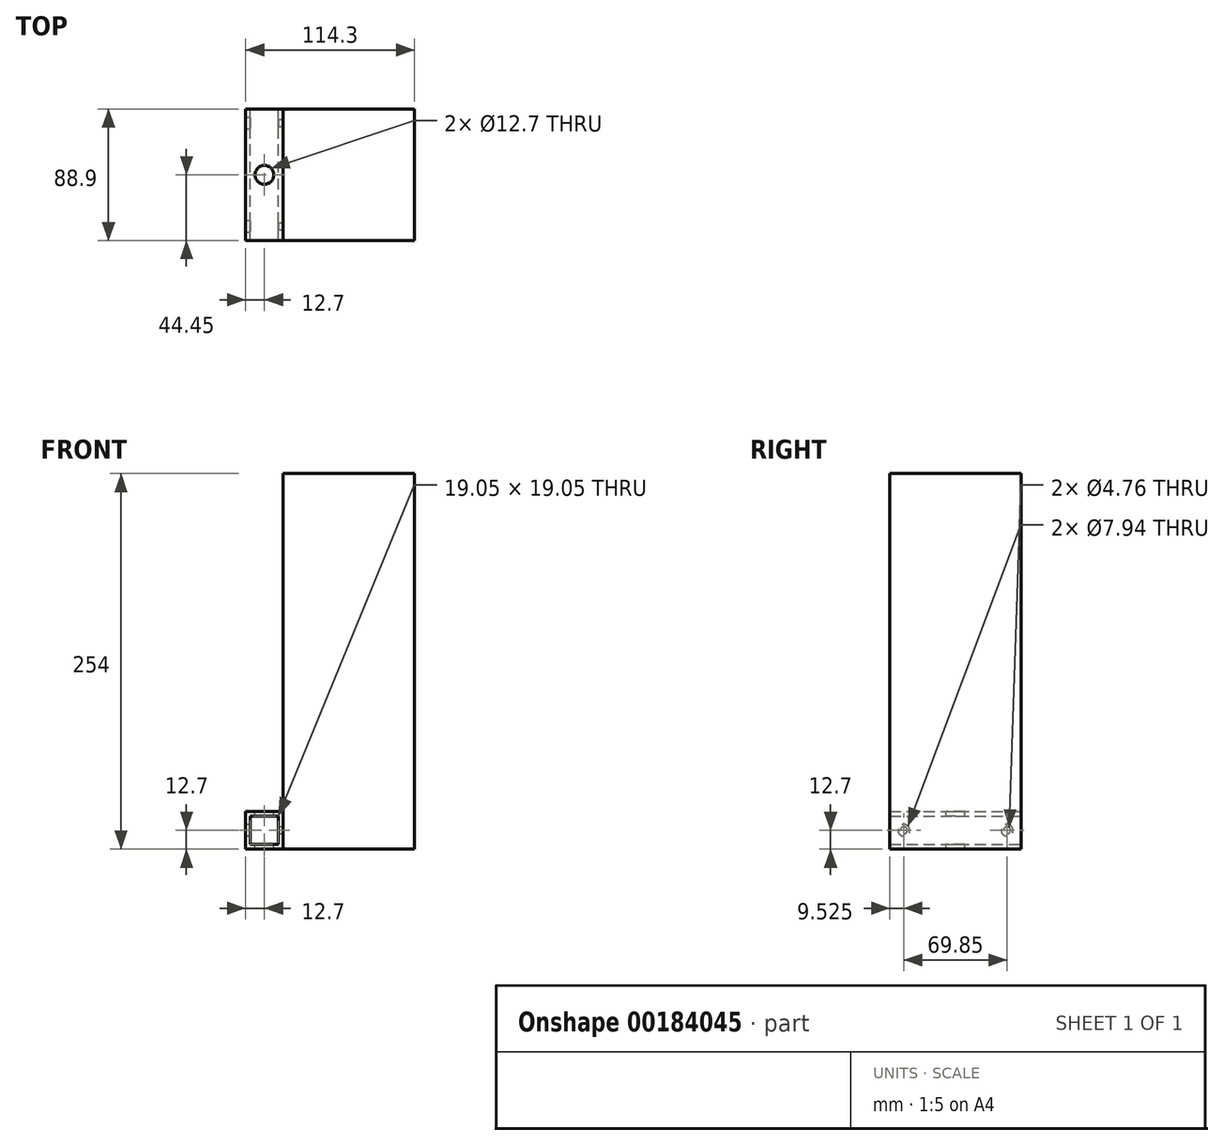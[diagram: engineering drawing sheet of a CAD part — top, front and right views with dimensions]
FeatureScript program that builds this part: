
annotation { "Feature Type Name" : "Feature", "Feature Type Description" : "" }
export const myFeature = defineFeature(function(context is Context, id is Id, definition is map)
    precondition{}
    {
        {
            var Q0;
            Q0=qCreatedBy(makeId("Front.planeOp"),FACE);
            var sketch = newSketch(context, id + "F0", { "sketchPlane" : qUnion([Q0])});
            skLineSegment(sketch, "E0.bottom", {"start": v(12.7, -12.7) * mm, "end": v(-12.7, -12.7) * mm});
            skLineSegment(sketch, "E0.top", {"start": v(12.7, 12.7) * mm, "end": v(-12.7, 12.7) * mm});
            skLineSegment(sketch, "E0.left", {"start": v(12.7, -12.7) * mm, "end": v(12.7, 12.7) * mm});
            skLineSegment(sketch, "E0.right", {"start": v(-12.7, -12.7) * mm, "end": v(-12.7, 12.7) * mm});
            skPoint(sketch, "E0.middle", {"position": v(0, 0) * mm});
            skLineSegment(sketch, "E1.0", {"start": v(9.53, 9.53) * mm, "end": v(-9.53, 9.52) * mm});
            skLineSegment(sketch, "E1.1", {"start": v(9.53, -9.53) * mm, "end": v(9.53, 9.53) * mm});
            skLineSegment(sketch, "E1.2", {"start": v(9.53, -9.53) * mm, "end": v(-9.53, -9.53) * mm});
            skLineSegment(sketch, "E1.3", {"start": v(-9.53, -9.53) * mm, "end": v(-9.53, 9.53) * mm});
            skSolve(sketch);
        }
        {
            var Q0;
            Q0=makeQuery(id+"F0.imprint","IMPRINT",FACE,{"disambiguationData":[TD([[makeQuery(id+"F0.imprint","IMPRINT",EDGE,{"derivedFrom":sQuery(id+"F0.wireOp",EDGE,"E0.bottom")}),-1.0]])]});
            var Q1;
            Q1=sQuery(id+"F0.wireOp",EDGE,"E0.right");
            var Q2;
            Q2=sQuery(id+"F0.wireOp",EDGE,"E0.top");
            var Q3;
            Q3=sQuery(id+"F0.wireOp",EDGE,"E0.left");
            var Q4;
            Q4=sQuery(id+"F0.wireOp",EDGE,"E0.bottom");
            extrude(context, id + "F1", {"entities" : qUnion([Q0]), "surfaceEntities" : qUnion([Q1, Q2, Q3, Q4]), "depth" : 88.9 * mm});
        }
        {
            var Q0;
            Q0=makeQuery(id+"F1.opExtrude","SWEPT_FACE",FACE,{"disambiguationData":[OSD([sQuery(id+"F0.wireOp",EDGE,"E0.top")])]});
            var sketch = newSketch(context, id + "F2", { "sketchPlane" : qUnion([Q0])});
            skCircle(sketch, "E2", {"center": v(0, -44.45) * mm, "radius": 6.35 * mm});
            skLineSegment(sketch, "E3", {"start": v(0, -88.9) * mm, "end": v(0, 0) * mm, "construction": true});
            skSolve(sketch);
        }
        {
            var Q0;
            Q0 = qSketchRegion(id + "F2", true);
            extrude(context, id + "F3", {"entities" : qUnion([Q0]), "operationType" : NewBodyOperationType.REMOVE, "endBound" : BoundingType.THROUGH_ALL, "oppositeDirection" : true, "depth" : 25.4 * mm});
        }
        {
            var Q0;
            Q0=makeQuery(id+"F1.opExtrude","SWEPT_FACE",FACE,{"disambiguationData":[OSD([sQuery(id+"F0.wireOp",EDGE,"E0.right")])]});
            var sketch = newSketch(context, id + "F4", { "sketchPlane" : qUnion([Q0])});
            skLineSegment(sketch, "E4.1", {"start": v(79.38, 0) * mm, "end": v(9.53, 0) * mm, "construction": true});
            skCircle(sketch, "E5", {"center": v(9.53, 0) * mm, "radius": 2.38 * mm});
            skCircle(sketch, "E6", {"center": v(79.38, 0) * mm, "radius": 2.38 * mm});
            skLineSegment(sketch, "E7", {"start": v(9.53, 0) * mm, "end": v(0, 0) * mm, "construction": true});
            skLineSegment(sketch, "E8", {"start": v(44.45, 0) * mm, "end": v(44.45, 12.7) * mm, "construction": true});
            skSolve(sketch);
        }
        {
            var Q0;
            Q0 = qSketchRegion(id + "F4", true);
            extrude(context, id + "F5", {"entities" : qUnion([Q0]), "operationType" : NewBodyOperationType.REMOVE, "endBound" : BoundingType.THROUGH_ALL, "oppositeDirection" : true, "depth" : 25.4 * mm});
        }
        {
            var Q0;
            Q0=makeQuery(id+"F1.opExtrude","SWEPT_FACE",FACE,{"disambiguationData":[OSD([sQuery(id+"F0.wireOp",EDGE,"E0.right")])]});
            var sketch = newSketch(context, id + "F6", { "sketchPlane" : qUnion([Q0])});
            skCircle(sketch, "E9", {"center": v(9.53, 0) * mm, "radius": 3.97 * mm});
            skCircle(sketch, "E10", {"center": v(79.38, 0) * mm, "radius": 3.97 * mm});
            skSolve(sketch);
        }
        {
            var Q0;
            Q0 = qSketchRegion(id + "F6", true);
            var Q1;
            Q1=makeQuery(id+"F1.opExtrude","SWEPT_FACE",FACE,{"disambiguationData":[OSD([sQuery(id+"F0.wireOp",EDGE,"E1.3")])]});
            extrude(context, id + "F7", {"entities" : qUnion([Q0]), "operationType" : NewBodyOperationType.REMOVE, "endBound" : BoundingType.UP_TO_SURFACE, "oppositeDirection" : true, "endBoundEntityFace" : qUnion([Q1]), "depth" : 25.4 * mm});
        }
        {
            var Q0;
            Q0=makeQuery(id+"F1.opExtrude","SWEPT_FACE",FACE,{"disambiguationData":[OSD([sQuery(id+"F0.wireOp",EDGE,"E0.bottom")])]});
            var sketch = newSketch(context, id + "F8", { "sketchPlane" : qUnion([Q0])});
            skLineSegment(sketch, "E11.bottom", {"start": v(12.7, 88.9) * mm, "end": v(101.6, 88.9) * mm});
            skLineSegment(sketch, "E11.top", {"start": v(12.7, 0) * mm, "end": v(101.6, 0) * mm});
            skLineSegment(sketch, "E11.left", {"start": v(12.7, 88.9) * mm, "end": v(12.7, 0) * mm});
            skLineSegment(sketch, "E11.right", {"start": v(101.6, 88.9) * mm, "end": v(101.6, 0) * mm});
            skSolve(sketch);
        }
        {
            var Q0;
            Q0 = qSketchRegion(id + "F8", true);
            extrude(context, id + "F9", {"entities" : qUnion([Q0]), "oppositeDirection" : true, "depth" : 254 * mm});
        }
    });
